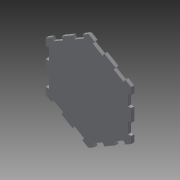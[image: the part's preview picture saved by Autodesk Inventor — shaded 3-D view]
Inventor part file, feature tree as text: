
AUTODESK INVENTOR PART (.ipt)
format: ipt  version: 2015 (Build 190159000, 159)  size: 142,848 bytes
history: native  units: mm
features: extrude x1, sketch x1
ambient origin geometry x8: Origin, YZ Plane, XZ Plane, XY Plane, X Axis, Y Axis, Z Axis, Center Point
bodies: Solid1 (feature_tree)
feature tree (2):
  extrude  "Extrusion1"  Depth=5.5mm
  sketch  "Sketch1"  dims[d4=150.0mm d6=86.60254mm d7=5.5mm d8=180.0deg d9=20.0mm d10=20.0mm d11=60.0mm d13=360.0deg d15=5.5mm d16=0.0mm]
